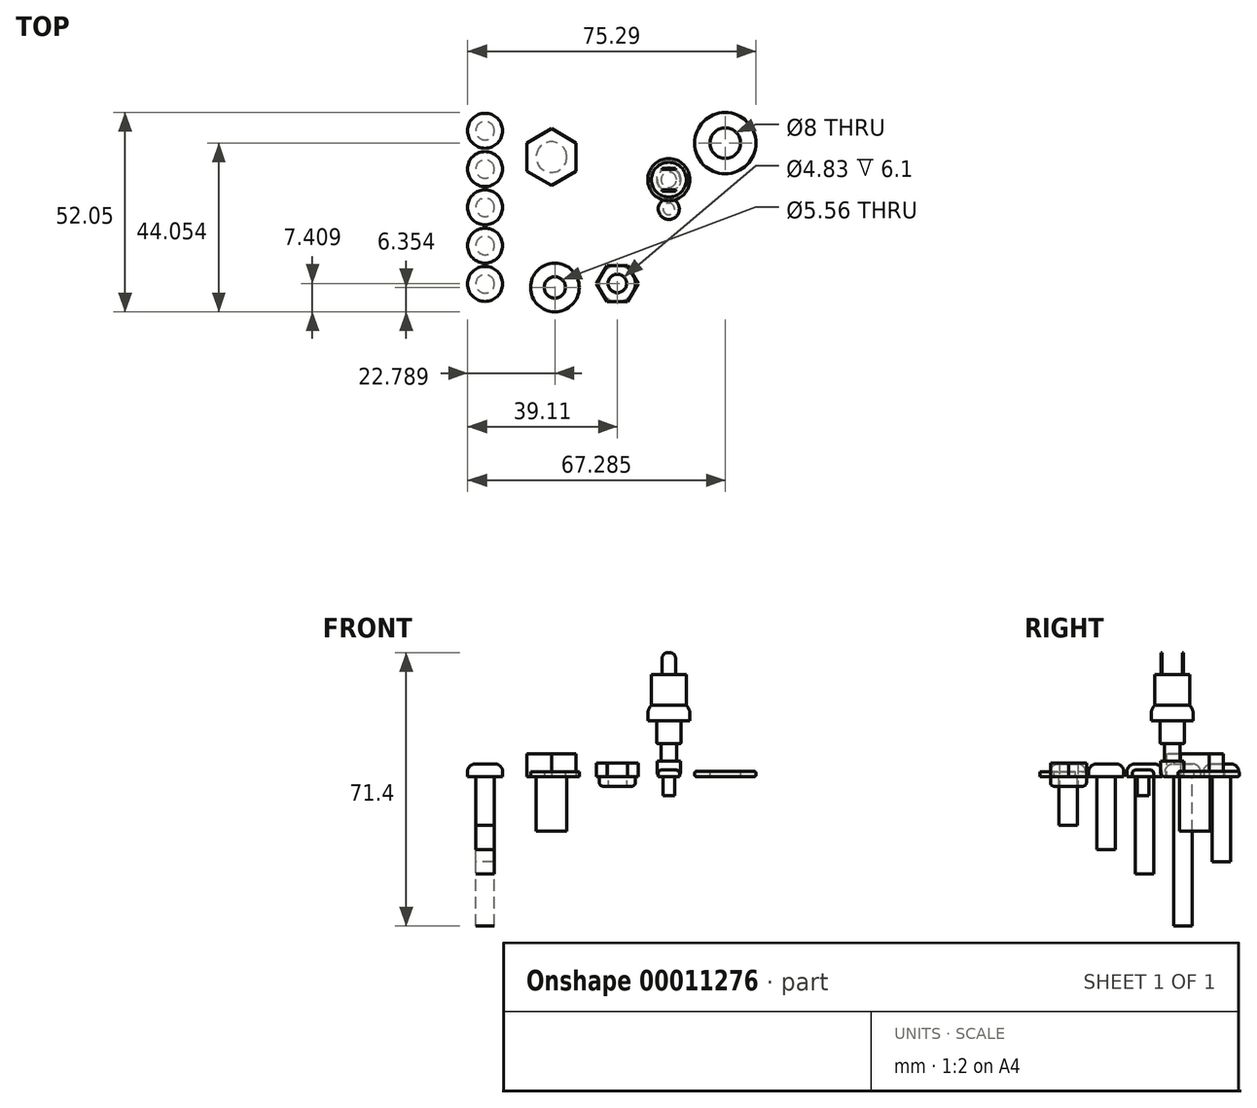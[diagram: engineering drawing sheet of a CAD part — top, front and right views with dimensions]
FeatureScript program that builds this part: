
annotation { "Feature Type Name" : "Feature", "Feature Type Description" : "" }
export const myFeature = defineFeature(function(context is Context, id is Id, definition is map)
    precondition{}
    {
        {
            var Q0;
            Q0=qCreatedBy(makeId("Top.planeOp"),FACE);
            var sketch = newSketch(context, id + "F0", { "sketchPlane" : qUnion([Q0])});
            skCircle(sketch, "E0", {"center": v(0, 0) * mm, "radius": 3 * mm});
            skSolve(sketch);
        }
        {
            var Q0;
            Q0 = qSketchRegion(id + "F0", true);
            extrude(context, id + "F1", {"entities" : qUnion([Q0]), "depth" : 4 * mm});
        }
        {
            var Q0;
            Q0=makeQuery(id+"F1.opExtrude","CAP_FACE",FACE,{"disambiguationData":[OSD([sQuery(id+"F0.wireOp",EDGE,"E0")])],"isStart":false});
            var sketch = newSketch(context, id + "F2", { "sketchPlane" : qUnion([Q0])});
            skCircle(sketch, "E1", {"center": v(0, 0) * mm, "radius": 2 * mm});
            skSolve(sketch);
        }
        {
            var Q0;
            Q0 = qSketchRegion(id + "F2", true);
            extrude(context, id + "F3", {"entities" : qUnion([Q0]), "operationType" : NewBodyOperationType.ADD, "depth" : 4.6 * mm});
        }
        {
            var Q0;
            Q0=makeQuery(id+"F3.opExtrude","CAP_FACE",FACE,{"disambiguationData":[OSD([sQuery(id+"F2.wireOp",EDGE,"E1")])],"isStart":false});
            var sketch = newSketch(context, id + "F4", { "sketchPlane" : qUnion([Q0])});
            skCircle(sketch, "E2", {"center": v(0, 0) * mm, "radius": 3.17 * mm});
            skSolve(sketch);
        }
        {
            var Q0;
            Q0 = qSketchRegion(id + "F4", true);
            extrude(context, id + "F5", {"entities" : qUnion([Q0]), "operationType" : NewBodyOperationType.ADD, "depth" : 6 * mm});
        }
        {
            var Q0;
            Q0=makeQuery(id+"F5.opExtrude","CAP_FACE",FACE,{"disambiguationData":[OSD([sQuery(id+"F4.wireOp",EDGE,"E2")])],"isStart":false});
            var sketch = newSketch(context, id + "F6", { "sketchPlane" : qUnion([Q0])});
            skCircle(sketch, "E3", {"center": v(0, 0) * mm, "radius": 5.5 * mm});
            skSolve(sketch);
        }
        {
            var Q0;
            Q0 = qSketchRegion(id + "F6", true);
            extrude(context, id + "F7", {"entities" : qUnion([Q0]), "operationType" : NewBodyOperationType.ADD, "depth" : 4 * mm});
        }
        {
            var Q0;
            Q0=makeQuery(id+"F7.opExtrude","CAP_FACE",FACE,{"disambiguationData":[OSD([sQuery(id+"F6.wireOp",EDGE,"E3")])],"isStart":false});
            var sketch = newSketch(context, id + "F8", { "sketchPlane" : qUnion([Q0])});
            skCircle(sketch, "E4", {"center": v(0, 0) * mm, "radius": 4.56 * mm});
            skSolve(sketch);
        }
        {
            var Q0;
            Q0=makeQuery(id+"F8.imprint","IMPRINT",FACE,{"disambiguationData":[TD([[makeQuery(id+"F8.imprint","IMPRINT",EDGE,{"derivedFrom":sQuery(id+"F8.wireOp",EDGE,"E4")}),1.0]])]});
            extrude(context, id + "F9", {"entities" : qUnion([Q0]), "operationType" : NewBodyOperationType.ADD, "depth" : 8 * mm});
        }
        {
            var Q0;
            Q0=makeQuery(id+"F7.opExtrude","CAP_EDGE",EDGE,{"disambiguationData":[OSD([sQuery(id+"F6.wireOp",EDGE,"E3")])],"isStart":false});
            fillet(context, id + "F10", {"entities" : qUnion([Q0]), "radius" : 3.2 * mm, "tangentPropagation" : true, "allowEdgeOverflow" : false});
        }
        {
            var Q0;
            Q0=makeQuery(id+"F1.opExtrude","CAP_EDGE",EDGE,{"disambiguationData":[OSD([sQuery(id+"F0.wireOp",EDGE,"E0")])],"isStart":true});
            fillet(context, id + "F11", {"entities" : qUnion([Q0]), "radius" : 1 * mm, "tangentPropagation" : true, "allowEdgeOverflow" : false});
        }
        {
            var Q0;
            Q0=makeQuery(id+"F5.opExtrude","CAP_EDGE",EDGE,{"disambiguationData":[OSD([sQuery(id+"F4.wireOp",EDGE,"E2")])],"isStart":true});
            fillet(context, id + "F12", {"entities" : qUnion([Q0]), "radius" : .3 * mm, "tangentPropagation" : true, "allowEdgeOverflow" : false});
        }
        {
            var Q0;
            Q0=makeQuery(id+"F9.opExtrude","CAP_FACE",FACE,{"disambiguationData":[OSD([sQuery(id+"F8.wireOp",EDGE,"E4")])],"isStart":false});
            var sketch = newSketch(context, id + "F13", { "sketchPlane" : qUnion([Q0])});
            skLineSegment(sketch, "E5.rect.bottom", {"start": v(1.75, 2.96) * mm, "end": v(-1.75, 2.96) * mm});
            skLineSegment(sketch, "E5.rect.top", {"start": v(1.75, -2.96) * mm, "end": v(-1.75, -2.96) * mm});
            skLineSegment(sketch, "E5.rect.left", {"start": v(1.75, 2.96) * mm, "end": v(1.75, 2.66) * mm});
            skLineSegment(sketch, "E5.rect.right", {"start": v(-1.75, 2.96) * mm, "end": v(-1.75, 2.66) * mm});
            skPoint(sketch, "E5.rect.middle", {"position": v(0, 0) * mm});
            skLineSegment(sketch, "E6", {"start": v(-1.75, -2.66) * mm, "end": v(1.75, -2.66) * mm});
            skLineSegment(sketch, "E7", {"start": v(-1.75, 2.66) * mm, "end": v(1.75, 2.66) * mm});
            skLineSegment(sketch, "E8.trimOffspring", {"start": v(-1.75, -2.66) * mm, "end": v(-1.75, -2.96) * mm});
            skLineSegment(sketch, "E9.trimOffspring", {"start": v(1.75, -2.66) * mm, "end": v(1.75, -2.96) * mm});
            skSolve(sketch);
        }
        {
            var Q0;
            Q0 = qSketchRegion(id + "F13", true);
            extrude(context, id + "F14", {"entities" : qUnion([Q0]), "operationType" : NewBodyOperationType.ADD, "depth" : 5.8 * mm});
        }
        {
            var Q0;
            Q0=makeQuery(id+"F14.opExtrude","CAP_EDGE",EDGE,{"disambiguationData":[OSD([sQuery(id+"F13.wireOp",EDGE,"E5.rect.left")])],"isStart":false});
            var Q1;
            Q1=makeQuery(id+"F14.opExtrude","CAP_EDGE",EDGE,{"disambiguationData":[OSD([sQuery(id+"F13.wireOp",EDGE,"E9.trimOffspring")])],"isStart":false});
            var Q2;
            Q2=makeQuery(id+"F14.opExtrude","CAP_EDGE",EDGE,{"disambiguationData":[OSD([sQuery(id+"F13.wireOp",EDGE,"E8.trimOffspring")])],"isStart":false});
            var Q3;
            Q3=makeQuery(id+"F14.opExtrude","CAP_EDGE",EDGE,{"disambiguationData":[OSD([sQuery(id+"F13.wireOp",EDGE,"E5.rect.right")])],"isStart":false});
            fillet(context, id + "F15", {"entities" : qUnion([Q0, Q1, Q2, Q3]), "radius" : 1.5 * mm, "tangentPropagation" : true, "allowEdgeOverflow" : false});
        }
        {
            var Q0;
            Q0=qCreatedBy(makeId("Top.planeOp"),FACE);
            var sketch = newSketch(context, id + "F16", { "sketchPlane" : qUnion([Q0])});
            skCircle(sketch, "E10", {"center": v(-47.98, -27.21) * mm, "radius": 2.41 * mm});
            skCircle(sketch, "E11", {"center": v(-47.98, -27.21) * mm, "radius": 4.57 * mm});
            skSolve(sketch);
        }
        {
            var Q0;
            Q0=makeQuery(id+"F16.imprint","IMPRINT",FACE,{"disambiguationData":[TD([[makeQuery(id+"F16.imprint","IMPRINT",EDGE,{"derivedFrom":sQuery(id+"F16.wireOp",EDGE,"E10")}),1.0]])]});
            var Q1;
            Q1=makeQuery(id+"F16.imprint","IMPRINT",FACE,{"disambiguationData":[TD([[makeQuery(id+"F16.imprint","IMPRINT",EDGE,{"derivedFrom":sQuery(id+"F16.wireOp",EDGE,"E10")}),-1.0]])]});
            extrude(context, id + "F17", {"entities" : qUnion([Q0, Q1]), "depth" : 3.3 * mm});
        }
        {
            var Q0;
            Q0=makeQuery(id+"F17.opExtrude","CAP_EDGE",EDGE,{"disambiguationData":[OSD([sQuery(id+"F16.wireOp",EDGE,"E11")])],"isStart":false});
            fillet(context, id + "F18", {"entities" : qUnion([Q0]), "radius" : 2 * mm, "tangentPropagation" : true, "allowEdgeOverflow" : false});
        }
        {
            var Q0;
            Q0=makeQuery(id+"F16.imprint","IMPRINT",FACE,{"disambiguationData":[TD([[makeQuery(id+"F16.imprint","IMPRINT",EDGE,{"derivedFrom":sQuery(id+"F16.wireOp",EDGE,"E10")}),1.0]])]});
            extrude(context, id + "F19", {"entities" : qUnion([Q0]), "operationType" : NewBodyOperationType.ADD, "oppositeDirection" : true, "depth" : 1 * mm});
        }
        {
            var Q0;
            Q0=makeQuery(id+"F17.opExtrude","SWEPT_BODY",BODY,{"disambiguationData":[OSD([sQuery(id+"F16.wireOp",EDGE,"E11")])]});
            transform(context, id + "F20", {"entities" : qUnion([Q0]), "transformType" : TransformType.TRANSLATION_3D, "dx" : 0 * mm, "dy" : 10 * mm, "dz" : 0 * mm, "makeCopy" : true});
        }
        {
            var Q0;
            Q0=makeQuery(id+"F19.opExtrude","CAP_FACE",FACE,{"disambiguationData":[OSD([sQuery(id+"F16.wireOp",EDGE,"E10")])],"isStart":false});
            extrude(context, id + "F21", {"entities" : qUnion([Q0]), "operationType" : NewBodyOperationType.ADD, "depth" : 11.7 * mm});
        }
        {
            var Q0;
            Q0=makeQuery(id+"F20.opPattern","COPY",BODY,{"derivedFrom":makeQuery(id+"F17.opExtrude","SWEPT_BODY",BODY,{"disambiguationData":[OSD([sQuery(id+"F16.wireOp",EDGE,"E11")])]}),"instanceName":"1"});
            transform(context, id + "F22", {"entities" : qUnion([Q0]), "transformType" : TransformType.TRANSLATION_3D, "dx" : 0 * mm, "dy" : 10 * mm, "dz" : 0 * mm, "makeCopy" : true});
        }
        {
            var Q0;
            Q0=makeQuery(id+"F20.opPattern","COPY",FACE,{"derivedFrom":makeQuery(id+"F19.opExtrude","CAP_FACE",FACE,{"disambiguationData":[OSD([sQuery(id+"F16.wireOp",EDGE,"E10")])],"isStart":false}),"instanceName":"1"});
            extrude(context, id + "F23", {"entities" : qUnion([Q0]), "operationType" : NewBodyOperationType.ADD, "depth" : 18.05 * mm});
        }
        {
            var Q0;
            Q0=makeQuery(id+"F22.opPattern","COPY",BODY,{"derivedFrom":makeQuery(id+"F20.opPattern","COPY",BODY,{"derivedFrom":makeQuery(id+"F17.opExtrude","SWEPT_BODY",BODY,{"disambiguationData":[OSD([sQuery(id+"F16.wireOp",EDGE,"E11")])]}),"instanceName":"1"}),"instanceName":"1"});
            transform(context, id + "F24", {"entities" : qUnion([Q0]), "transformType" : TransformType.TRANSLATION_3D, "dx" : 0 * mm, "dy" : 10 * mm, "dz" : 0 * mm, "makeCopy" : true});
        }
        {
            var Q0;
            Q0=makeQuery(id+"F22.opPattern","COPY",FACE,{"derivedFrom":makeQuery(id+"F20.opPattern","COPY",FACE,{"derivedFrom":makeQuery(id+"F19.opExtrude","CAP_FACE",FACE,{"disambiguationData":[OSD([sQuery(id+"F16.wireOp",EDGE,"E10")])],"isStart":false}),"instanceName":"1"}),"instanceName":"1"});
            extrude(context, id + "F25", {"entities" : qUnion([Q0]), "operationType" : NewBodyOperationType.ADD, "depth" : 24.4 * mm});
        }
        {
            var Q0;
            Q0=makeQuery(id+"F24.opPattern","COPY",BODY,{"derivedFrom":makeQuery(id+"F22.opPattern","COPY",BODY,{"derivedFrom":makeQuery(id+"F20.opPattern","COPY",BODY,{"derivedFrom":makeQuery(id+"F17.opExtrude","SWEPT_BODY",BODY,{"disambiguationData":[OSD([sQuery(id+"F16.wireOp",EDGE,"E11")])]}),"instanceName":"1"}),"instanceName":"1"}),"instanceName":"1"});
            transform(context, id + "F26", {"entities" : qUnion([Q0]), "transformType" : TransformType.TRANSLATION_3D, "dx" : 0 * mm, "dy" : 10 * mm, "dz" : 0 * mm, "makeCopy" : true});
        }
        {
            var Q0;
            Q0=makeQuery(id+"F24.opPattern","COPY",FACE,{"derivedFrom":makeQuery(id+"F22.opPattern","COPY",FACE,{"derivedFrom":makeQuery(id+"F20.opPattern","COPY",FACE,{"derivedFrom":makeQuery(id+"F19.opExtrude","CAP_FACE",FACE,{"disambiguationData":[OSD([sQuery(id+"F16.wireOp",EDGE,"E10")])],"isStart":false}),"instanceName":"1"}),"instanceName":"1"}),"instanceName":"1"});
            extrude(context, id + "F27", {"entities" : qUnion([Q0]), "operationType" : NewBodyOperationType.ADD, "depth" : 38 * mm});
        }
        {
            var Q0;
            Q0=qCreatedBy(makeId("Top.planeOp"),FACE);
            var sketch = newSketch(context, id + "F28", { "sketchPlane" : qUnion([Q0])});
            skCircle(sketch, "E12", {"center": v(-29.76, -28.15) * mm, "radius": 2.78 * mm});
            skCircle(sketch, "E13", {"center": v(-29.76, -28.15) * mm, "radius": 6.35 * mm});
            skSolve(sketch);
        }
        {
            var Q0;
            Q0 = qSketchRegion(id + "F28", true);
            extrude(context, id + "F29", {"entities" : qUnion([Q0]), "depth" : 1.23 * mm});
        }
        {
            var Q0;
            Q0=qCreatedBy(makeId("Top.planeOp"),FACE);
            var sketch = newSketch(context, id + "F30", { "sketchPlane" : qUnion([Q0])});
            skCircle(sketch, "E14.cCircle", {"center": v(-13.44, -27.1) * mm, "radius": 4.7 * mm, "construction": true});
            skLineSegment(sketch, "E14.0", {"start": v(-16.15, -22.4) * mm, "end": v(-10.73, -22.4) * mm});
            skLineSegment(sketch, "E14.1", {"start": v(-10.73, -22.4) * mm, "end": v(-8.01, -27.1) * mm});
            skLineSegment(sketch, "E14.2", {"start": v(-8.01, -27.1) * mm, "end": v(-10.73, -31.79) * mm});
            skLineSegment(sketch, "E14.3", {"start": v(-10.73, -31.79) * mm, "end": v(-16.15, -31.79) * mm});
            skLineSegment(sketch, "E14.4", {"start": v(-16.15, -31.79) * mm, "end": v(-18.87, -27.1) * mm});
            skLineSegment(sketch, "E14.5", {"start": v(-18.87, -27.1) * mm, "end": v(-16.15, -22.4) * mm});
            skPoint(sketch, "E14.0.midPoint", {"position": v(-13.44, -22.4) * mm});
            skCircle(sketch, "E15", {"center": v(-13.44, -27.1) * mm, "radius": 2.41 * mm});
            skCircle(sketch, "E16", {"center": v(-13.44, -27.1) * mm, "radius": 4.7 * mm});
            skSolve(sketch);
        }
        {
            var Q0;
            Q0 = qSketchRegion(id + "F30", true);
            extrude(context, id + "F31", {"entities" : qUnion([Q0]), "depth" : 3.56 * mm});
        }
        {
            var Q0;
            Q0=makeQuery(id+"F30.imprint","IMPRINT",FACE,{"disambiguationData":[TD([[makeQuery(id+"F30.imprint","IMPRINT",EDGE,{"derivedFrom":sQuery(id+"F30.wireOp",EDGE,"E15")}),-1.0]])]});
            extrude(context, id + "F32", {"entities" : qUnion([Q0]), "operationType" : NewBodyOperationType.ADD, "oppositeDirection" : true, "depth" : 2.54 * mm});
        }
        {
            var Q0;
            Q0=makeQuery(id+"F32.opExtrude","CAP_EDGE",EDGE,{"disambiguationData":[OSD([sQuery(id+"F30.wireOp",EDGE,"E16")])],"isStart":false});
            fillet(context, id + "F33", {"entities" : qUnion([Q0]), "radius" : 1 * mm, "tangentPropagation" : true, "allowEdgeOverflow" : false});
        }
        {
            var Q0;
            Q0=makeQuery(id+"F26.opPattern","COPY",FACE,{"derivedFrom":makeQuery(id+"F24.opPattern","COPY",FACE,{"derivedFrom":makeQuery(id+"F22.opPattern","COPY",FACE,{"derivedFrom":makeQuery(id+"F20.opPattern","COPY",FACE,{"derivedFrom":makeQuery(id+"F19.opExtrude","CAP_FACE",FACE,{"disambiguationData":[OSD([sQuery(id+"F16.wireOp",EDGE,"E10")])],"isStart":false}),"instanceName":"1"}),"instanceName":"1"}),"instanceName":"1"}),"instanceName":"1"});
            extrude(context, id + "F34", {"entities" : qUnion([Q0]), "operationType" : NewBodyOperationType.ADD, "depth" : 21.23 * mm});
        }
        {
            var Q0;
            Q0=qCreatedBy(makeId("Top.planeOp"),FACE);
            var sketch = newSketch(context, id + "F35", { "sketchPlane" : qUnion([Q0])});
            skCircle(sketch, "E17.cCircle", {"center": v(-30.65, 5.93) * mm, "radius": 6.4 * mm, "construction": true});
            skLineSegment(sketch, "E17.0", {"start": v(-24.25, 9.62) * mm, "end": v(-24.25, 2.23) * mm});
            skLineSegment(sketch, "E17.1", {"start": v(-24.25, 2.23) * mm, "end": v(-30.65, -1.46) * mm});
            skLineSegment(sketch, "E17.2", {"start": v(-30.65, -1.46) * mm, "end": v(-37.05, 2.23) * mm});
            skLineSegment(sketch, "E17.3", {"start": v(-37.05, 2.23) * mm, "end": v(-37.05, 9.62) * mm});
            skLineSegment(sketch, "E17.4", {"start": v(-37.05, 9.62) * mm, "end": v(-30.65, 13.32) * mm});
            skLineSegment(sketch, "E17.5", {"start": v(-30.65, 13.32) * mm, "end": v(-24.25, 9.62) * mm});
            skPoint(sketch, "E17.0.midPoint", {"position": v(-24.25, 5.93) * mm});
            skCircle(sketch, "E18", {"center": v(-30.65, 5.93) * mm, "radius": 4 * mm});
            skSolve(sketch);
        }
        {
            var Q0;
            Q0 = qSketchRegion(id + "F35", true);
            var Q1;
            Q1=makeQuery(id+"F35.imprint","IMPRINT",FACE,{"disambiguationData":[TD([[makeQuery(id+"F35.imprint","IMPRINT",EDGE,{"derivedFrom":sQuery(id+"F35.wireOp",EDGE,"E18")}),1.0]])]});
            extrude(context, id + "F36", {"entities" : qUnion([Q0, Q1]), "depth" : 6 * mm});
        }
        {
            var Q0;
            Q0=makeQuery(id+"F35.imprint","IMPRINT",FACE,{"disambiguationData":[TD([[makeQuery(id+"F35.imprint","IMPRINT",EDGE,{"derivedFrom":sQuery(id+"F35.wireOp",EDGE,"E18")}),1.0]])]});
            var Q1;
            Q1=sQuery(id+"F35.wireOp",EDGE,"E18");
            extrude(context, id + "F37", {"entities" : qUnion([Q0]), "operationType" : NewBodyOperationType.ADD, "surfaceEntities" : qUnion([Q1]), "oppositeDirection" : true, "depth" : 14.29 * mm});
        }
        {
            var Q0;
            Q0=qCreatedBy(makeId("Top.planeOp"),FACE);
            var sketch = newSketch(context, id + "F46", { "sketchPlane" : qUnion([Q0])});
            skCircle(sketch, "E19", {"center": v(0, -7.62) * mm, "radius": 1.5 * mm});
            skCircle(sketch, "E20", {"center": v(0, -7.62) * mm, "radius": 2.75 * mm});
            skSolve(sketch);
        }
        {
            var Q0;
            Q0=makeQuery(id+"F46.imprint","IMPRINT",FACE,{"disambiguationData":[TD([[makeQuery(id+"F46.imprint","IMPRINT",EDGE,{"derivedFrom":sQuery(id+"F46.wireOp",EDGE,"E19")}),-1.0]])]});
            var Q1;
            Q1=makeQuery(id+"F46.imprint","IMPRINT",FACE,{"disambiguationData":[TD([[makeQuery(id+"F46.imprint","IMPRINT",EDGE,{"derivedFrom":sQuery(id+"F46.wireOp",EDGE,"E19")}),1.0]])]});
            extrude(context, id + "F47", {"entities" : qUnion([Q0, Q1]), "depth" : 1.7 * mm});
        }
        {
            var Q0;
            Q0=makeQuery(id+"F46.imprint","IMPRINT",FACE,{"disambiguationData":[TD([[makeQuery(id+"F46.imprint","IMPRINT",EDGE,{"derivedFrom":sQuery(id+"F46.wireOp",EDGE,"E19")}),1.0]])]});
            extrude(context, id + "F38", {"entities" : qUnion([Q0]), "operationType" : NewBodyOperationType.ADD, "oppositeDirection" : true, "depth" : 5 * mm});
        }
        {
            var Q0;
            Q0=makeQuery(id+"F47.opExtrude","CAP_EDGE",EDGE,{"disambiguationData":[OSD([sQuery(id+"F46.wireOp",EDGE,"E20")])],"isStart":false});
            fillet(context, id + "F39", {"entities" : qUnion([Q0]), "radius" : 0.75 * mm, "tangentPropagation" : true, "allowEdgeOverflow" : false});
        }
        {
            var Q0;
            Q0=makeQuery(id+"F36.opExtrude","SWEPT_BODY",BODY,{"disambiguationData":[OSD([sQuery(id+"F35.wireOp",EDGE,"E17.0"),sQuery(id+"F35.wireOp",EDGE,"E17.1"),sQuery(id+"F35.wireOp",EDGE,"E17.2"),sQuery(id+"F35.wireOp",EDGE,"E17.3"),sQuery(id+"F35.wireOp",EDGE,"E17.4"),sQuery(id+"F35.wireOp",EDGE,"E17.5")])]});
            transform(context, id + "F40", {"entities" : qUnion([Q0]), "transformType" : TransformType.TRANSLATION_3D, "dx" : 20.5 * mm, "dy" : 0 * mm, "dz" : 0 * mm, "makeCopy" : true});
        }
        {
            var Q0;
            Q0=makeQuery(id+"F40.opPattern","COPY",FACE,{"derivedFrom":makeQuery(id+"F37.opExtrude","CAP_FACE",FACE,{"disambiguationData":[OSD([sQuery(id+"F35.wireOp",EDGE,"E18")])],"isStart":false}),"instanceName":"1"});
            extrude(context, id + "F41", {"entities" : qUnion([Q0]), "operationType" : NewBodyOperationType.ADD, "depth" : 11.1 * mm});
        }
        {
            var Q0;
            Q0=qCreatedBy(makeId("Top.planeOp"),FACE);
            var sketch = newSketch(context, id + "F42", { "sketchPlane" : qUnion([Q0])});
            skCircle(sketch, "E21", {"center": v(14.74, 9.55) * mm, "radius": 4 * mm});
            skCircle(sketch, "E22", {"center": v(14.74, 9.55) * mm, "radius": 8 * mm});
            skSolve(sketch);
        }
        {
            var Q0;
            Q0 = qSketchRegion(id + "F42", true);
            extrude(context, id + "F43", {"entities" : qUnion([Q0]), "depth" : 1.4 * mm});
        }
        {
            var Q0;
            Q0=makeQuery(id+"F43.opExtrude","CAP_EDGE",EDGE,{"disambiguationData":[OSD([sQuery(id+"F42.wireOp",EDGE,"E22")])],"isStart":true});
            var Q1;
            Q1=makeQuery(id+"F43.opExtrude","CAP_EDGE",EDGE,{"disambiguationData":[OSD([sQuery(id+"F42.wireOp",EDGE,"E22")])],"isStart":false});
            fillet(context, id + "F44", {"entities" : qUnion([Q0, Q1]), "radius" : .5 * mm, "tangentPropagation" : true, "allowEdgeOverflow" : false});
        }
        {
            var Q0;
            Q0=makeQuery(id+"F40.opPattern","COPY",BODY,{"derivedFrom":makeQuery(id+"F36.opExtrude","SWEPT_BODY",BODY,{"disambiguationData":[OSD([sQuery(id+"F35.wireOp",EDGE,"E17.0"),sQuery(id+"F35.wireOp",EDGE,"E17.1"),sQuery(id+"F35.wireOp",EDGE,"E17.2"),sQuery(id+"F35.wireOp",EDGE,"E17.3"),sQuery(id+"F35.wireOp",EDGE,"E17.4"),sQuery(id+"F35.wireOp",EDGE,"E17.5")])]}),"instanceName":"1"});
            deleteBodies(context, id + "F45", {"entities" : qUnion([Q0])});
        }
    });
